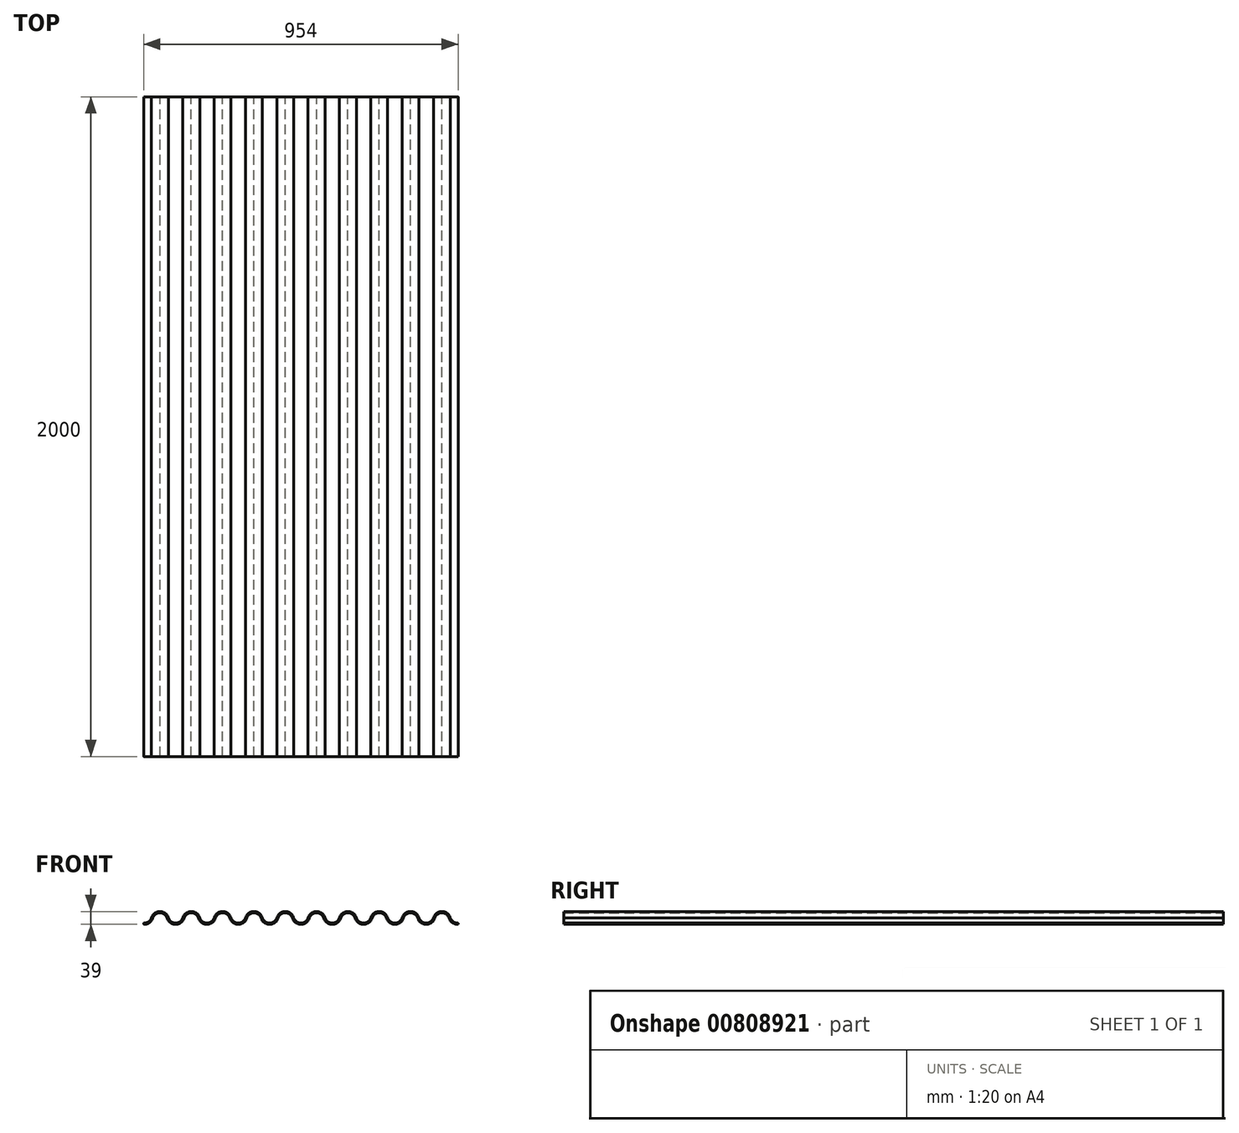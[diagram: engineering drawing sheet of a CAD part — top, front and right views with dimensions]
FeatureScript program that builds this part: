
annotation { "Feature Type Name" : "Feature", "Feature Type Description" : "" }
export const myFeature = defineFeature(function(context is Context, id is Id, definition is map)
    precondition{}
    {
        {
            var Q0;
            Q0=qCreatedBy(makeId("Front.planeOp"),FACE);
            var sketch = newSketch(context, id + "F0", { "sketchPlane" : qUnion([Q0])});
            skLineSegment(sketch, "E0.bottom", {"start": v(0, 0) * mm, "end": v(95, 0) * mm, "construction": true});
            skLineSegment(sketch, "E0.top", {"start": v(0, 35) * mm, "end": v(95, 35) * mm, "construction": true});
            skLineSegment(sketch, "E0.left", {"start": v(0, 0) * mm, "end": v(0, 35) * mm, "construction": true});
            skLineSegment(sketch, "E0.right", {"start": v(95, 0) * mm, "end": v(95, 35) * mm, "construction": true});
            skLineSegment(sketch, "E1", {"start": v(0, 17.5) * mm, "end": v(95, 17.5) * mm, "construction": true});
            skLineSegment(sketch, "E2", {"start": v(47.5, 35) * mm, "end": v(47.5, 0) * mm, "construction": true});
            skLineSegment(sketch, "E3", {"start": v(23.75, 35) * mm, "end": v(23.75, 0) * mm, "construction": true});
            skLineSegment(sketch, "E4", {"start": v(71.25, 35) * mm, "end": v(71.25, 0) * mm, "construction": true});
            skSolve(sketch);
        }
        {
            var Q0;
            Q0=qCreatedBy(makeId("Front.planeOp"),FACE);
            var sketch = newSketch(context, id + "F1", { "sketchPlane" : qUnion([Q0])});
            skArc(sketch, "E5", {"start": v(71.25, 17.2) * mm, "mid": v(62.3, 30) * mm, "end": v(47.5, 35) * mm});
            skArc(sketch, "E6", {"start": v(0, 0) * mm, "mid": v(14.66, 4.75) * mm, "end": v(23.75, 17.2) * mm});
            skArc(sketch, "E7", {"start": v(47.5, 35) * mm, "mid": v(32.7, 30) * mm, "end": v(23.75, 17.2) * mm});
            skArc(sketch, "E8", {"start": v(71.25, 17.2) * mm, "mid": v(80.34, 4.75) * mm, "end": v(95, 0) * mm});
            skArc(sketch, "E9.MirrorCS", {"start": v(0, 0) * mm, "mid": v(-14.66, 4.75) * mm, "end": v(-23.75, 17.2) * mm});
            skArc(sketch, "E10.MirrorCS", {"start": v(-71.25, 17.2) * mm, "mid": v(-80.34, 4.75) * mm, "end": v(-95, 0) * mm});
            skArc(sketch, "E11.MirrorCS", {"start": v(-47.5, 35) * mm, "mid": v(-32.7, 30) * mm, "end": v(-23.75, 17.2) * mm});
            skArc(sketch, "E12.MirrorCS", {"start": v(-71.25, 17.2) * mm, "mid": v(-62.3, 30) * mm, "end": v(-47.5, 35) * mm});
            skArc(sketch, "E13", {"start": v(261.25, 17.2) * mm, "mid": v(252.3, 30) * mm, "end": v(237.5, 35) * mm});
            skArc(sketch, "E14", {"start": v(190, 0) * mm, "mid": v(204.66, 4.75) * mm, "end": v(213.75, 17.2) * mm});
            skArc(sketch, "E15", {"start": v(237.5, 35) * mm, "mid": v(222.7, 30) * mm, "end": v(213.75, 17.2) * mm});
            skArc(sketch, "E16", {"start": v(261.25, 17.2) * mm, "mid": v(270.34, 4.75) * mm, "end": v(285, 0) * mm});
            skArc(sketch, "E17.MirrorCS", {"start": v(190, 0) * mm, "mid": v(175.34, 4.75) * mm, "end": v(166.25, 17.2) * mm});
            skArc(sketch, "E18.MirrorCS", {"start": v(118.75, 17.2) * mm, "mid": v(109.66, 4.75) * mm, "end": v(95, 0) * mm});
            skArc(sketch, "E19.MirrorCS", {"start": v(142.5, 35) * mm, "mid": v(157.3, 30) * mm, "end": v(166.25, 17.2) * mm});
            skArc(sketch, "E20.MirrorCS", {"start": v(118.75, 17.2) * mm, "mid": v(127.7, 30) * mm, "end": v(142.5, 35) * mm});
            skArc(sketch, "E21", {"start": v(451.25, 17.2) * mm, "mid": v(442.3, 30) * mm, "end": v(427.5, 35) * mm});
            skArc(sketch, "E22", {"start": v(380, 0) * mm, "mid": v(394.66, 4.75) * mm, "end": v(403.75, 17.2) * mm});
            skArc(sketch, "E23", {"start": v(427.5, 35) * mm, "mid": v(412.7, 30) * mm, "end": v(403.75, 17.2) * mm});
            skArc(sketch, "E24", {"start": v(451.25, 17.2) * mm, "mid": v(460.34, 4.75) * mm, "end": v(475, 0) * mm});
            skArc(sketch, "E25.MirrorCS", {"start": v(380, 0) * mm, "mid": v(365.34, 4.75) * mm, "end": v(356.25, 17.2) * mm});
            skArc(sketch, "E26.MirrorCS", {"start": v(308.75, 17.2) * mm, "mid": v(299.66, 4.75) * mm, "end": v(285, 0) * mm});
            skArc(sketch, "E27.MirrorCS", {"start": v(332.5, 35) * mm, "mid": v(347.3, 30) * mm, "end": v(356.25, 17.2) * mm});
            skArc(sketch, "E28.MirrorCS", {"start": v(308.75, 17.2) * mm, "mid": v(317.7, 30) * mm, "end": v(332.5, 35) * mm});
            skArc(sketch, "E29", {"start": v(641.25, 17.2) * mm, "mid": v(632.3, 30) * mm, "end": v(617.5, 35) * mm});
            skArc(sketch, "E30", {"start": v(570, 0) * mm, "mid": v(584.66, 4.75) * mm, "end": v(593.75, 17.2) * mm});
            skArc(sketch, "E31", {"start": v(617.5, 35) * mm, "mid": v(602.7, 30) * mm, "end": v(593.75, 17.2) * mm});
            skArc(sketch, "E32", {"start": v(641.25, 17.2) * mm, "mid": v(650.34, 4.75) * mm, "end": v(665, 0) * mm});
            skArc(sketch, "E33.MirrorCS", {"start": v(570, 0) * mm, "mid": v(555.34, 4.75) * mm, "end": v(546.25, 17.2) * mm});
            skArc(sketch, "E34.MirrorCS", {"start": v(498.75, 17.2) * mm, "mid": v(489.66, 4.75) * mm, "end": v(475, 0) * mm});
            skArc(sketch, "E35.MirrorCS", {"start": v(522.5, 35) * mm, "mid": v(537.3, 30) * mm, "end": v(546.25, 17.2) * mm});
            skArc(sketch, "E36.MirrorCS", {"start": v(498.75, 17.2) * mm, "mid": v(507.7, 30) * mm, "end": v(522.5, 35) * mm});
            skArc(sketch, "E37", {"start": v(831.25, 17.2) * mm, "mid": v(822.3, 30) * mm, "end": v(807.5, 35) * mm});
            skArc(sketch, "E38", {"start": v(760, 0) * mm, "mid": v(774.66, 4.75) * mm, "end": v(783.75, 17.2) * mm});
            skArc(sketch, "E39", {"start": v(807.5, 35) * mm, "mid": v(792.7, 30) * mm, "end": v(783.75, 17.2) * mm});
            skArc(sketch, "E40", {"start": v(831.25, 17.2) * mm, "mid": v(840.34, 4.75) * mm, "end": v(855, 0) * mm});
            skArc(sketch, "E41.MirrorCS", {"start": v(760, 0) * mm, "mid": v(745.34, 4.75) * mm, "end": v(736.25, 17.2) * mm});
            skArc(sketch, "E42.MirrorCS", {"start": v(688.75, 17.2) * mm, "mid": v(679.66, 4.75) * mm, "end": v(665, 0) * mm});
            skArc(sketch, "E43.MirrorCS", {"start": v(712.5, 35) * mm, "mid": v(727.3, 30) * mm, "end": v(736.25, 17.2) * mm});
            skArc(sketch, "E44.MirrorCS", {"start": v(688.75, 17.2) * mm, "mid": v(697.7, 30) * mm, "end": v(712.5, 35) * mm});
            skArc(sketch, "E45.0.startCap", {"start": v(760, 2) * mm, "mid": v(762, 0) * mm, "end": v(760, -2) * mm});
            skArc(sketch, "E45.0.endCap", {"start": v(734.35, 16.57) * mm, "mid": v(735.63, 19.1) * mm, "end": v(738.15, 17.82) * mm});
            skArc(sketch, "E45.0.left", {"start": v(760, -2) * mm, "mid": v(744.17, 3.13) * mm, "end": v(734.35, 16.57) * mm});
            skArc(sketch, "E45.0.right", {"start": v(760, 2) * mm, "mid": v(746.51, 6.37) * mm, "end": v(738.15, 17.82) * mm});
            skArc(sketch, "E45.1.startCap", {"start": v(380, 2) * mm, "mid": v(382, 0) * mm, "end": v(380, -2) * mm});
            skArc(sketch, "E45.1.endCap", {"start": v(354.35, 16.57) * mm, "mid": v(355.63, 19.1) * mm, "end": v(358.15, 17.82) * mm});
            skArc(sketch, "E45.1.left", {"start": v(380, -2) * mm, "mid": v(364.17, 3.13) * mm, "end": v(354.35, 16.57) * mm});
            skArc(sketch, "E45.1.right", {"start": v(380, 2) * mm, "mid": v(366.51, 6.37) * mm, "end": v(358.15, 17.82) * mm});
            skArc(sketch, "E45.2.startCap", {"start": v(190, 2) * mm, "mid": v(192, 0) * mm, "end": v(190, -2) * mm});
            skArc(sketch, "E45.2.endCap", {"start": v(164.35, 16.57) * mm, "mid": v(165.63, 19.1) * mm, "end": v(168.15, 17.82) * mm});
            skArc(sketch, "E45.2.left", {"start": v(190, -2) * mm, "mid": v(174.17, 3.13) * mm, "end": v(164.35, 16.57) * mm});
            skArc(sketch, "E45.2.right", {"start": v(190, 2) * mm, "mid": v(176.51, 6.37) * mm, "end": v(168.15, 17.82) * mm});
            skArc(sketch, "E45.3.startCap", {"start": v(570, 2) * mm, "mid": v(572, 0) * mm, "end": v(570, -2) * mm});
            skArc(sketch, "E45.3.endCap", {"start": v(544.35, 16.57) * mm, "mid": v(545.63, 19.1) * mm, "end": v(548.15, 17.82) * mm});
            skArc(sketch, "E45.3.left", {"start": v(570, -2) * mm, "mid": v(554.17, 3.13) * mm, "end": v(544.35, 16.57) * mm});
            skArc(sketch, "E45.3.right", {"start": v(570, 2) * mm, "mid": v(556.51, 6.37) * mm, "end": v(548.15, 17.82) * mm});
            skArc(sketch, "E45.4.startCap", {"start": v(639.35, 16.57) * mm, "mid": v(640.63, 19.1) * mm, "end": v(643.15, 17.82) * mm});
            skArc(sketch, "E45.4.endCap", {"start": v(665, 2) * mm, "mid": v(667, 0) * mm, "end": v(665, -2) * mm});
            skArc(sketch, "E45.4.left", {"start": v(643.15, 17.82) * mm, "mid": v(651.51, 6.37) * mm, "end": v(665, 2) * mm});
            skArc(sketch, "E45.4.right", {"start": v(639.35, 16.57) * mm, "mid": v(649.17, 3.13) * mm, "end": v(665, -2) * mm});
            skArc(sketch, "E45.5.startCap", {"start": v(449.35, 16.57) * mm, "mid": v(450.63, 19.1) * mm, "end": v(453.15, 17.82) * mm});
            skArc(sketch, "E45.5.endCap", {"start": v(475, 2) * mm, "mid": v(477, 0) * mm, "end": v(475, -2) * mm});
            skArc(sketch, "E45.5.left", {"start": v(453.15, 17.82) * mm, "mid": v(461.51, 6.37) * mm, "end": v(475, 2) * mm});
            skArc(sketch, "E45.5.right", {"start": v(449.35, 16.57) * mm, "mid": v(459.17, 3.13) * mm, "end": v(475, -2) * mm});
            skArc(sketch, "E45.6.startCap", {"start": v(259.35, 16.57) * mm, "mid": v(260.63, 19.1) * mm, "end": v(263.15, 17.82) * mm});
            skArc(sketch, "E45.6.endCap", {"start": v(285, 2) * mm, "mid": v(287, 0) * mm, "end": v(285, -2) * mm});
            skArc(sketch, "E45.6.left", {"start": v(263.15, 17.82) * mm, "mid": v(271.51, 6.37) * mm, "end": v(285, 2) * mm});
            skArc(sketch, "E45.6.right", {"start": v(259.35, 16.57) * mm, "mid": v(269.17, 3.13) * mm, "end": v(285, -2) * mm});
            skArc(sketch, "E45.7.startCap", {"start": v(829.35, 16.57) * mm, "mid": v(830.63, 19.1) * mm, "end": v(833.15, 17.82) * mm});
            skArc(sketch, "E45.7.endCap", {"start": v(855, 2) * mm, "mid": v(857, 0) * mm, "end": v(855, -2) * mm});
            skArc(sketch, "E45.7.left", {"start": v(833.15, 17.82) * mm, "mid": v(841.51, 6.37) * mm, "end": v(855, 2) * mm});
            skArc(sketch, "E45.7.right", {"start": v(829.35, 16.57) * mm, "mid": v(839.17, 3.13) * mm, "end": v(855, -2) * mm});
            skArc(sketch, "E45.8.startCap", {"start": v(310.67, 16.62) * mm, "mid": v(308.17, 15.28) * mm, "end": v(306.83, 17.77) * mm});
            skArc(sketch, "E45.8.endCap", {"start": v(332.48, 37) * mm, "mid": v(334.5, 35.02) * mm, "end": v(332.52, 33) * mm});
            skArc(sketch, "E45.8.left", {"start": v(306.83, 17.77) * mm, "mid": v(316.5, 31.6) * mm, "end": v(332.48, 37) * mm});
            skArc(sketch, "E45.8.right", {"start": v(310.67, 16.62) * mm, "mid": v(318.9, 28.4) * mm, "end": v(332.52, 33) * mm});
            skArc(sketch, "E45.9.startCap", {"start": v(120.67, 16.62) * mm, "mid": v(118.17, 15.28) * mm, "end": v(116.83, 17.77) * mm});
            skArc(sketch, "E45.9.endCap", {"start": v(142.48, 37) * mm, "mid": v(144.5, 35.02) * mm, "end": v(142.52, 33) * mm});
            skArc(sketch, "E45.9.left", {"start": v(116.83, 17.77) * mm, "mid": v(126.5, 31.6) * mm, "end": v(142.48, 37) * mm});
            skArc(sketch, "E45.9.right", {"start": v(120.67, 16.62) * mm, "mid": v(128.9, 28.4) * mm, "end": v(142.52, 33) * mm});
            skArc(sketch, "E45.10.startCap", {"start": v(690.67, 16.62) * mm, "mid": v(688.17, 15.28) * mm, "end": v(686.83, 17.77) * mm});
            skArc(sketch, "E45.10.endCap", {"start": v(712.48, 37) * mm, "mid": v(714.5, 35.02) * mm, "end": v(712.52, 33) * mm});
            skArc(sketch, "E45.10.left", {"start": v(686.83, 17.77) * mm, "mid": v(696.5, 31.6) * mm, "end": v(712.48, 37) * mm});
            skArc(sketch, "E45.10.right", {"start": v(690.67, 16.62) * mm, "mid": v(698.9, 28.4) * mm, "end": v(712.52, 33) * mm});
            skArc(sketch, "E45.11.startCap", {"start": v(500.67, 16.62) * mm, "mid": v(498.17, 15.28) * mm, "end": v(496.83, 17.77) * mm});
            skArc(sketch, "E45.11.endCap", {"start": v(522.48, 37) * mm, "mid": v(524.5, 35.02) * mm, "end": v(522.52, 33) * mm});
            skArc(sketch, "E45.11.left", {"start": v(496.83, 17.77) * mm, "mid": v(506.5, 31.6) * mm, "end": v(522.48, 37) * mm});
            skArc(sketch, "E45.11.right", {"start": v(500.67, 16.62) * mm, "mid": v(508.9, 28.4) * mm, "end": v(522.52, 33) * mm});
            skArc(sketch, "E45.12.startCap", {"start": v(0, 2) * mm, "mid": v(2, 0) * mm, "end": v(0, -2) * mm});
            skArc(sketch, "E45.12.endCap", {"start": v(-25.65, 16.57) * mm, "mid": v(-24.37, 19.1) * mm, "end": v(-21.85, 17.82) * mm});
            skArc(sketch, "E45.12.left", {"start": v(0, -2) * mm, "mid": v(-15.83, 3.13) * mm, "end": v(-25.65, 16.57) * mm});
            skArc(sketch, "E45.12.right", {"start": v(0, 2) * mm, "mid": v(-13.49, 6.37) * mm, "end": v(-21.85, 17.82) * mm});
            skArc(sketch, "E45.13.startCap", {"start": v(833.17, 17.77) * mm, "mid": v(831.83, 15.28) * mm, "end": v(829.33, 16.62) * mm});
            skArc(sketch, "E45.13.endCap", {"start": v(807.48, 33) * mm, "mid": v(805.5, 35.02) * mm, "end": v(807.52, 37) * mm});
            skArc(sketch, "E45.13.left", {"start": v(829.33, 16.62) * mm, "mid": v(821.1, 28.4) * mm, "end": v(807.48, 33) * mm});
            skArc(sketch, "E45.13.right", {"start": v(833.17, 17.77) * mm, "mid": v(823.5, 31.6) * mm, "end": v(807.52, 37) * mm});
            skArc(sketch, "E45.14.startCap", {"start": v(686.85, 17.82) * mm, "mid": v(689.37, 19.1) * mm, "end": v(690.65, 16.57) * mm});
            skArc(sketch, "E45.14.endCap", {"start": v(665, -2) * mm, "mid": v(663, 0) * mm, "end": v(665, 2) * mm});
            skArc(sketch, "E45.14.left", {"start": v(690.65, 16.57) * mm, "mid": v(680.83, 3.13) * mm, "end": v(665, -2) * mm});
            skArc(sketch, "E45.14.right", {"start": v(686.85, 17.82) * mm, "mid": v(678.49, 6.37) * mm, "end": v(665, 2) * mm});
            skArc(sketch, "E45.15.startCap", {"start": v(496.85, 17.82) * mm, "mid": v(499.37, 19.1) * mm, "end": v(500.65, 16.57) * mm});
            skArc(sketch, "E45.15.endCap", {"start": v(475, -2) * mm, "mid": v(473, 0) * mm, "end": v(475, 2) * mm});
            skArc(sketch, "E45.15.left", {"start": v(500.65, 16.57) * mm, "mid": v(490.83, 3.13) * mm, "end": v(475, -2) * mm});
            skArc(sketch, "E45.15.right", {"start": v(496.85, 17.82) * mm, "mid": v(488.49, 6.37) * mm, "end": v(475, 2) * mm});
            skArc(sketch, "E45.16.startCap", {"start": v(643.17, 17.77) * mm, "mid": v(641.83, 15.28) * mm, "end": v(639.33, 16.62) * mm});
            skArc(sketch, "E45.16.endCap", {"start": v(617.48, 33) * mm, "mid": v(615.5, 35.02) * mm, "end": v(617.52, 37) * mm});
            skArc(sketch, "E45.16.left", {"start": v(639.33, 16.62) * mm, "mid": v(631.1, 28.4) * mm, "end": v(617.48, 33) * mm});
            skArc(sketch, "E45.16.right", {"start": v(643.17, 17.77) * mm, "mid": v(633.5, 31.6) * mm, "end": v(617.52, 37) * mm});
            skArc(sketch, "E45.17.startCap", {"start": v(306.85, 17.82) * mm, "mid": v(309.37, 19.1) * mm, "end": v(310.65, 16.57) * mm});
            skArc(sketch, "E45.17.endCap", {"start": v(285, -2) * mm, "mid": v(283, 0) * mm, "end": v(285, 2) * mm});
            skArc(sketch, "E45.17.left", {"start": v(310.65, 16.57) * mm, "mid": v(300.83, 3.13) * mm, "end": v(285, -2) * mm});
            skArc(sketch, "E45.17.right", {"start": v(306.85, 17.82) * mm, "mid": v(298.49, 6.37) * mm, "end": v(285, 2) * mm});
            skArc(sketch, "E45.18.startCap", {"start": v(116.85, 17.82) * mm, "mid": v(119.37, 19.1) * mm, "end": v(120.65, 16.57) * mm});
            skArc(sketch, "E45.18.endCap", {"start": v(95, -2) * mm, "mid": v(93, 0) * mm, "end": v(95, 2) * mm});
            skArc(sketch, "E45.18.left", {"start": v(120.65, 16.57) * mm, "mid": v(110.83, 3.13) * mm, "end": v(95, -2) * mm});
            skArc(sketch, "E45.18.right", {"start": v(116.85, 17.82) * mm, "mid": v(108.49, 6.37) * mm, "end": v(95, 2) * mm});
            skArc(sketch, "E45.19.startCap", {"start": v(453.17, 17.77) * mm, "mid": v(451.83, 15.28) * mm, "end": v(449.33, 16.62) * mm});
            skArc(sketch, "E45.19.endCap", {"start": v(427.48, 33) * mm, "mid": v(425.5, 35.02) * mm, "end": v(427.52, 37) * mm});
            skArc(sketch, "E45.19.left", {"start": v(449.33, 16.62) * mm, "mid": v(441.1, 28.4) * mm, "end": v(427.48, 33) * mm});
            skArc(sketch, "E45.19.right", {"start": v(453.17, 17.77) * mm, "mid": v(443.5, 31.6) * mm, "end": v(427.52, 37) * mm});
            skArc(sketch, "E45.20.startCap", {"start": v(263.17, 17.77) * mm, "mid": v(261.83, 15.28) * mm, "end": v(259.33, 16.62) * mm});
            skArc(sketch, "E45.20.endCap", {"start": v(237.48, 33) * mm, "mid": v(235.5, 35.02) * mm, "end": v(237.52, 37) * mm});
            skArc(sketch, "E45.20.left", {"start": v(259.33, 16.62) * mm, "mid": v(251.1, 28.4) * mm, "end": v(237.48, 33) * mm});
            skArc(sketch, "E45.20.right", {"start": v(263.17, 17.77) * mm, "mid": v(253.5, 31.6) * mm, "end": v(237.52, 37) * mm});
            skArc(sketch, "E45.21.startCap", {"start": v(-69.33, 16.62) * mm, "mid": v(-71.83, 15.28) * mm, "end": v(-73.17, 17.77) * mm});
            skArc(sketch, "E45.21.endCap", {"start": v(-47.52, 37) * mm, "mid": v(-45.5, 35.02) * mm, "end": v(-47.48, 33) * mm});
            skArc(sketch, "E45.21.left", {"start": v(-73.17, 17.77) * mm, "mid": v(-63.5, 31.6) * mm, "end": v(-47.52, 37) * mm});
            skArc(sketch, "E45.21.right", {"start": v(-69.33, 16.62) * mm, "mid": v(-61.1, 28.4) * mm, "end": v(-47.48, 33) * mm});
            skArc(sketch, "E45.22.startCap", {"start": v(-47.52, 33) * mm, "mid": v(-49.5, 35.02) * mm, "end": v(-47.48, 37) * mm});
            skArc(sketch, "E45.22.endCap", {"start": v(-21.83, 17.77) * mm, "mid": v(-23.17, 15.28) * mm, "end": v(-25.67, 16.62) * mm});
            skArc(sketch, "E45.22.left", {"start": v(-47.48, 37) * mm, "mid": v(-31.5, 31.6) * mm, "end": v(-21.83, 17.77) * mm});
            skArc(sketch, "E45.22.right", {"start": v(-47.52, 33) * mm, "mid": v(-33.9, 28.4) * mm, "end": v(-25.67, 16.62) * mm});
            skArc(sketch, "E45.23.startCap", {"start": v(73.17, 17.77) * mm, "mid": v(71.83, 15.28) * mm, "end": v(69.33, 16.62) * mm});
            skArc(sketch, "E45.23.endCap", {"start": v(47.48, 33) * mm, "mid": v(45.5, 35.02) * mm, "end": v(47.52, 37) * mm});
            skArc(sketch, "E45.23.left", {"start": v(69.33, 16.62) * mm, "mid": v(61.1, 28.4) * mm, "end": v(47.48, 33) * mm});
            skArc(sketch, "E45.23.right", {"start": v(73.17, 17.77) * mm, "mid": v(63.5, 31.6) * mm, "end": v(47.52, 37) * mm});
            skArc(sketch, "E45.24.startCap", {"start": v(-73.15, 17.82) * mm, "mid": v(-70.63, 19.1) * mm, "end": v(-69.35, 16.57) * mm});
            skArc(sketch, "E45.24.endCap", {"start": v(-95, -2) * mm, "mid": v(-97, 0) * mm, "end": v(-95, 2) * mm});
            skArc(sketch, "E45.24.left", {"start": v(-69.35, 16.57) * mm, "mid": v(-79.17, 3.13) * mm, "end": v(-95, -2) * mm});
            skArc(sketch, "E45.24.right", {"start": v(-73.15, 17.82) * mm, "mid": v(-81.51, 6.37) * mm, "end": v(-95, 2) * mm});
            skArc(sketch, "E45.25.startCap", {"start": v(47.48, 37) * mm, "mid": v(49.5, 35.02) * mm, "end": v(47.52, 33) * mm});
            skArc(sketch, "E45.25.endCap", {"start": v(25.67, 16.62) * mm, "mid": v(23.17, 15.28) * mm, "end": v(21.83, 17.77) * mm});
            skArc(sketch, "E45.25.left", {"start": v(47.52, 33) * mm, "mid": v(33.9, 28.4) * mm, "end": v(25.67, 16.62) * mm});
            skArc(sketch, "E45.25.right", {"start": v(47.48, 37) * mm, "mid": v(31.5, 31.6) * mm, "end": v(21.83, 17.77) * mm});
            skArc(sketch, "E45.26.startCap", {"start": v(332.48, 33) * mm, "mid": v(330.5, 35.02) * mm, "end": v(332.52, 37) * mm});
            skArc(sketch, "E45.26.endCap", {"start": v(358.17, 17.77) * mm, "mid": v(356.83, 15.28) * mm, "end": v(354.33, 16.62) * mm});
            skArc(sketch, "E45.26.left", {"start": v(332.52, 37) * mm, "mid": v(348.5, 31.6) * mm, "end": v(358.17, 17.77) * mm});
            skArc(sketch, "E45.26.right", {"start": v(332.48, 33) * mm, "mid": v(346.1, 28.4) * mm, "end": v(354.33, 16.62) * mm});
            skArc(sketch, "E45.27.startCap", {"start": v(142.48, 33) * mm, "mid": v(140.5, 35.02) * mm, "end": v(142.52, 37) * mm});
            skArc(sketch, "E45.27.endCap", {"start": v(168.17, 17.77) * mm, "mid": v(166.83, 15.28) * mm, "end": v(164.33, 16.62) * mm});
            skArc(sketch, "E45.27.left", {"start": v(142.52, 37) * mm, "mid": v(158.5, 31.6) * mm, "end": v(168.17, 17.77) * mm});
            skArc(sketch, "E45.27.right", {"start": v(142.48, 33) * mm, "mid": v(156.1, 28.4) * mm, "end": v(164.33, 16.62) * mm});
            skArc(sketch, "E45.28.startCap", {"start": v(712.48, 33) * mm, "mid": v(710.5, 35.02) * mm, "end": v(712.52, 37) * mm});
            skArc(sketch, "E45.28.endCap", {"start": v(738.17, 17.77) * mm, "mid": v(736.83, 15.28) * mm, "end": v(734.33, 16.62) * mm});
            skArc(sketch, "E45.28.left", {"start": v(712.52, 37) * mm, "mid": v(728.5, 31.6) * mm, "end": v(738.17, 17.77) * mm});
            skArc(sketch, "E45.28.right", {"start": v(712.48, 33) * mm, "mid": v(726.1, 28.4) * mm, "end": v(734.33, 16.62) * mm});
            skArc(sketch, "E45.29.startCap", {"start": v(522.48, 33) * mm, "mid": v(520.5, 35.02) * mm, "end": v(522.52, 37) * mm});
            skArc(sketch, "E45.29.endCap", {"start": v(548.17, 17.77) * mm, "mid": v(546.83, 15.28) * mm, "end": v(544.33, 16.62) * mm});
            skArc(sketch, "E45.29.left", {"start": v(522.52, 37) * mm, "mid": v(538.5, 31.6) * mm, "end": v(548.17, 17.77) * mm});
            skArc(sketch, "E45.29.right", {"start": v(522.48, 33) * mm, "mid": v(536.1, 28.4) * mm, "end": v(544.33, 16.62) * mm});
            skArc(sketch, "E45.30.startCap", {"start": v(380, -2) * mm, "mid": v(378, 0) * mm, "end": v(380, 2) * mm});
            skArc(sketch, "E45.30.endCap", {"start": v(401.85, 17.82) * mm, "mid": v(404.37, 19.1) * mm, "end": v(405.65, 16.57) * mm});
            skArc(sketch, "E45.30.left", {"start": v(380, 2) * mm, "mid": v(393.49, 6.37) * mm, "end": v(401.85, 17.82) * mm});
            skArc(sketch, "E45.30.right", {"start": v(380, -2) * mm, "mid": v(395.83, 3.13) * mm, "end": v(405.65, 16.57) * mm});
            skArc(sketch, "E45.31.startCap", {"start": v(190, -2) * mm, "mid": v(188, 0) * mm, "end": v(190, 2) * mm});
            skArc(sketch, "E45.31.endCap", {"start": v(211.85, 17.82) * mm, "mid": v(214.37, 19.1) * mm, "end": v(215.65, 16.57) * mm});
            skArc(sketch, "E45.31.left", {"start": v(190, 2) * mm, "mid": v(203.49, 6.37) * mm, "end": v(211.85, 17.82) * mm});
            skArc(sketch, "E45.31.right", {"start": v(190, -2) * mm, "mid": v(205.83, 3.13) * mm, "end": v(215.65, 16.57) * mm});
            skArc(sketch, "E45.32.startCap", {"start": v(760, -2) * mm, "mid": v(758, 0) * mm, "end": v(760, 2) * mm});
            skArc(sketch, "E45.32.endCap", {"start": v(781.85, 17.82) * mm, "mid": v(784.37, 19.1) * mm, "end": v(785.65, 16.57) * mm});
            skArc(sketch, "E45.32.left", {"start": v(760, 2) * mm, "mid": v(773.49, 6.37) * mm, "end": v(781.85, 17.82) * mm});
            skArc(sketch, "E45.32.right", {"start": v(760, -2) * mm, "mid": v(775.83, 3.13) * mm, "end": v(785.65, 16.57) * mm});
            skArc(sketch, "E45.33.startCap", {"start": v(570, -2) * mm, "mid": v(568, 0) * mm, "end": v(570, 2) * mm});
            skArc(sketch, "E45.33.endCap", {"start": v(591.85, 17.82) * mm, "mid": v(594.37, 19.1) * mm, "end": v(595.65, 16.57) * mm});
            skArc(sketch, "E45.33.left", {"start": v(570, 2) * mm, "mid": v(583.49, 6.37) * mm, "end": v(591.85, 17.82) * mm});
            skArc(sketch, "E45.33.right", {"start": v(570, -2) * mm, "mid": v(585.83, 3.13) * mm, "end": v(595.65, 16.57) * mm});
            skArc(sketch, "E45.34.startCap", {"start": v(807.48, 37) * mm, "mid": v(809.5, 35.02) * mm, "end": v(807.52, 33) * mm});
            skArc(sketch, "E45.34.endCap", {"start": v(785.67, 16.62) * mm, "mid": v(783.17, 15.28) * mm, "end": v(781.83, 17.77) * mm});
            skArc(sketch, "E45.34.left", {"start": v(807.52, 33) * mm, "mid": v(793.9, 28.4) * mm, "end": v(785.67, 16.62) * mm});
            skArc(sketch, "E45.34.right", {"start": v(807.48, 37) * mm, "mid": v(791.5, 31.6) * mm, "end": v(781.83, 17.77) * mm});
            skArc(sketch, "E45.35.startCap", {"start": v(617.48, 37) * mm, "mid": v(619.5, 35.02) * mm, "end": v(617.52, 33) * mm});
            skArc(sketch, "E45.35.endCap", {"start": v(595.67, 16.62) * mm, "mid": v(593.17, 15.28) * mm, "end": v(591.83, 17.77) * mm});
            skArc(sketch, "E45.35.left", {"start": v(617.52, 33) * mm, "mid": v(603.9, 28.4) * mm, "end": v(595.67, 16.62) * mm});
            skArc(sketch, "E45.35.right", {"start": v(617.48, 37) * mm, "mid": v(601.5, 31.6) * mm, "end": v(591.83, 17.77) * mm});
            skArc(sketch, "E45.36.startCap", {"start": v(427.48, 37) * mm, "mid": v(429.5, 35.02) * mm, "end": v(427.52, 33) * mm});
            skArc(sketch, "E45.36.endCap", {"start": v(405.67, 16.62) * mm, "mid": v(403.17, 15.28) * mm, "end": v(401.83, 17.77) * mm});
            skArc(sketch, "E45.36.left", {"start": v(427.52, 33) * mm, "mid": v(413.9, 28.4) * mm, "end": v(405.67, 16.62) * mm});
            skArc(sketch, "E45.36.right", {"start": v(427.48, 37) * mm, "mid": v(411.5, 31.6) * mm, "end": v(401.83, 17.77) * mm});
            skArc(sketch, "E45.37.startCap", {"start": v(237.48, 37) * mm, "mid": v(239.5, 35.02) * mm, "end": v(237.52, 33) * mm});
            skArc(sketch, "E45.37.endCap", {"start": v(215.67, 16.62) * mm, "mid": v(213.17, 15.28) * mm, "end": v(211.83, 17.77) * mm});
            skArc(sketch, "E45.37.left", {"start": v(237.52, 33) * mm, "mid": v(223.9, 28.4) * mm, "end": v(215.67, 16.62) * mm});
            skArc(sketch, "E45.37.right", {"start": v(237.48, 37) * mm, "mid": v(221.5, 31.6) * mm, "end": v(211.83, 17.77) * mm});
            skArc(sketch, "E45.38.startCap", {"start": v(116.85, 17.82) * mm, "mid": v(119.37, 19.1) * mm, "end": v(120.65, 16.57) * mm});
            skArc(sketch, "E45.38.endCap", {"start": v(95, -2) * mm, "mid": v(93, 0) * mm, "end": v(95, 2) * mm});
            skArc(sketch, "E45.38.left", {"start": v(120.65, 16.57) * mm, "mid": v(110.83, 3.13) * mm, "end": v(95, -2) * mm});
            skArc(sketch, "E45.38.right", {"start": v(116.85, 17.82) * mm, "mid": v(108.49, 6.37) * mm, "end": v(95, 2) * mm});
            skArc(sketch, "E45.39.startCap", {"start": v(142.48, 33) * mm, "mid": v(140.5, 35.02) * mm, "end": v(142.52, 37) * mm});
            skArc(sketch, "E45.39.endCap", {"start": v(168.17, 17.77) * mm, "mid": v(166.83, 15.28) * mm, "end": v(164.33, 16.62) * mm});
            skArc(sketch, "E45.39.left", {"start": v(142.52, 37) * mm, "mid": v(158.5, 31.6) * mm, "end": v(168.17, 17.77) * mm});
            skArc(sketch, "E45.39.right", {"start": v(142.48, 33) * mm, "mid": v(156.1, 28.4) * mm, "end": v(164.33, 16.62) * mm});
            skArc(sketch, "E45.40.startCap", {"start": v(332.48, 33) * mm, "mid": v(330.5, 35.02) * mm, "end": v(332.52, 37) * mm});
            skArc(sketch, "E45.40.endCap", {"start": v(358.17, 17.77) * mm, "mid": v(356.83, 15.28) * mm, "end": v(354.33, 16.62) * mm});
            skArc(sketch, "E45.40.left", {"start": v(332.52, 37) * mm, "mid": v(348.5, 31.6) * mm, "end": v(358.17, 17.77) * mm});
            skArc(sketch, "E45.40.right", {"start": v(332.48, 33) * mm, "mid": v(346.1, 28.4) * mm, "end": v(354.33, 16.62) * mm});
            skArc(sketch, "E45.41.startCap", {"start": v(712.48, 33) * mm, "mid": v(710.5, 35.02) * mm, "end": v(712.52, 37) * mm});
            skArc(sketch, "E45.41.endCap", {"start": v(738.17, 17.77) * mm, "mid": v(736.83, 15.28) * mm, "end": v(734.33, 16.62) * mm});
            skArc(sketch, "E45.41.left", {"start": v(712.52, 37) * mm, "mid": v(728.5, 31.6) * mm, "end": v(738.17, 17.77) * mm});
            skArc(sketch, "E45.41.right", {"start": v(712.48, 33) * mm, "mid": v(726.1, 28.4) * mm, "end": v(734.33, 16.62) * mm});
            skArc(sketch, "E45.42.startCap", {"start": v(449.35, 16.57) * mm, "mid": v(450.63, 19.1) * mm, "end": v(453.15, 17.82) * mm});
            skArc(sketch, "E45.42.endCap", {"start": v(475, 2) * mm, "mid": v(477, 0) * mm, "end": v(475, -2) * mm});
            skArc(sketch, "E45.42.left", {"start": v(453.15, 17.82) * mm, "mid": v(461.51, 6.37) * mm, "end": v(475, 2) * mm});
            skArc(sketch, "E45.42.right", {"start": v(449.35, 16.57) * mm, "mid": v(459.17, 3.13) * mm, "end": v(475, -2) * mm});
            skArc(sketch, "E45.43.startCap", {"start": v(522.48, 33) * mm, "mid": v(520.5, 35.02) * mm, "end": v(522.52, 37) * mm});
            skArc(sketch, "E45.43.endCap", {"start": v(548.17, 17.77) * mm, "mid": v(546.83, 15.28) * mm, "end": v(544.33, 16.62) * mm});
            skArc(sketch, "E45.43.left", {"start": v(522.52, 37) * mm, "mid": v(538.5, 31.6) * mm, "end": v(548.17, 17.77) * mm});
            skArc(sketch, "E45.43.right", {"start": v(522.48, 33) * mm, "mid": v(536.1, 28.4) * mm, "end": v(544.33, 16.62) * mm});
            skArc(sketch, "E45.44.startCap", {"start": v(639.35, 16.57) * mm, "mid": v(640.63, 19.1) * mm, "end": v(643.15, 17.82) * mm});
            skArc(sketch, "E45.44.endCap", {"start": v(665, 2) * mm, "mid": v(667, 0) * mm, "end": v(665, -2) * mm});
            skArc(sketch, "E45.44.left", {"start": v(643.15, 17.82) * mm, "mid": v(651.51, 6.37) * mm, "end": v(665, 2) * mm});
            skArc(sketch, "E45.44.right", {"start": v(639.35, 16.57) * mm, "mid": v(649.17, 3.13) * mm, "end": v(665, -2) * mm});
            skArc(sketch, "E45.45.startCap", {"start": v(829.35, 16.57) * mm, "mid": v(830.63, 19.1) * mm, "end": v(833.15, 17.82) * mm});
            skArc(sketch, "E45.45.endCap", {"start": v(855, 2) * mm, "mid": v(857, 0) * mm, "end": v(855, -2) * mm});
            skArc(sketch, "E45.45.left", {"start": v(833.15, 17.82) * mm, "mid": v(841.51, 6.37) * mm, "end": v(855, 2) * mm});
            skArc(sketch, "E45.45.right", {"start": v(829.35, 16.57) * mm, "mid": v(839.17, 3.13) * mm, "end": v(855, -2) * mm});
            skArc(sketch, "E45.46.startCap", {"start": v(306.85, 17.82) * mm, "mid": v(309.37, 19.1) * mm, "end": v(310.65, 16.57) * mm});
            skArc(sketch, "E45.46.endCap", {"start": v(285, -2) * mm, "mid": v(283, 0) * mm, "end": v(285, 2) * mm});
            skArc(sketch, "E45.46.left", {"start": v(310.65, 16.57) * mm, "mid": v(300.83, 3.13) * mm, "end": v(285, -2) * mm});
            skArc(sketch, "E45.46.right", {"start": v(306.85, 17.82) * mm, "mid": v(298.49, 6.37) * mm, "end": v(285, 2) * mm});
            skArc(sketch, "E45.47.startCap", {"start": v(833.17, 17.77) * mm, "mid": v(831.83, 15.28) * mm, "end": v(829.33, 16.62) * mm});
            skArc(sketch, "E45.47.endCap", {"start": v(807.48, 33) * mm, "mid": v(805.5, 35.02) * mm, "end": v(807.52, 37) * mm});
            skArc(sketch, "E45.47.left", {"start": v(829.33, 16.62) * mm, "mid": v(821.1, 28.4) * mm, "end": v(807.48, 33) * mm});
            skArc(sketch, "E45.47.right", {"start": v(833.17, 17.77) * mm, "mid": v(823.5, 31.6) * mm, "end": v(807.52, 37) * mm});
            skArc(sketch, "E45.48.startCap", {"start": v(643.17, 17.77) * mm, "mid": v(641.83, 15.28) * mm, "end": v(639.33, 16.62) * mm});
            skArc(sketch, "E45.48.endCap", {"start": v(617.48, 33) * mm, "mid": v(615.5, 35.02) * mm, "end": v(617.52, 37) * mm});
            skArc(sketch, "E45.48.left", {"start": v(639.33, 16.62) * mm, "mid": v(631.1, 28.4) * mm, "end": v(617.48, 33) * mm});
            skArc(sketch, "E45.48.right", {"start": v(643.17, 17.77) * mm, "mid": v(633.5, 31.6) * mm, "end": v(617.52, 37) * mm});
            skArc(sketch, "E45.49.startCap", {"start": v(263.17, 17.77) * mm, "mid": v(261.83, 15.28) * mm, "end": v(259.33, 16.62) * mm});
            skArc(sketch, "E45.49.endCap", {"start": v(237.48, 33) * mm, "mid": v(235.5, 35.02) * mm, "end": v(237.52, 37) * mm});
            skArc(sketch, "E45.49.left", {"start": v(259.33, 16.62) * mm, "mid": v(251.1, 28.4) * mm, "end": v(237.48, 33) * mm});
            skArc(sketch, "E45.49.right", {"start": v(263.17, 17.77) * mm, "mid": v(253.5, 31.6) * mm, "end": v(237.52, 37) * mm});
            skArc(sketch, "E45.50.startCap", {"start": v(453.17, 17.77) * mm, "mid": v(451.83, 15.28) * mm, "end": v(449.33, 16.62) * mm});
            skArc(sketch, "E45.50.endCap", {"start": v(427.48, 33) * mm, "mid": v(425.5, 35.02) * mm, "end": v(427.52, 37) * mm});
            skArc(sketch, "E45.50.left", {"start": v(449.33, 16.62) * mm, "mid": v(441.1, 28.4) * mm, "end": v(427.48, 33) * mm});
            skArc(sketch, "E45.50.right", {"start": v(453.17, 17.77) * mm, "mid": v(443.5, 31.6) * mm, "end": v(427.52, 37) * mm});
            skArc(sketch, "E45.51.startCap", {"start": v(259.35, 16.57) * mm, "mid": v(260.63, 19.1) * mm, "end": v(263.15, 17.82) * mm});
            skArc(sketch, "E45.51.endCap", {"start": v(285, 2) * mm, "mid": v(287, 0) * mm, "end": v(285, -2) * mm});
            skArc(sketch, "E45.51.left", {"start": v(263.15, 17.82) * mm, "mid": v(271.51, 6.37) * mm, "end": v(285, 2) * mm});
            skArc(sketch, "E45.51.right", {"start": v(259.35, 16.57) * mm, "mid": v(269.17, 3.13) * mm, "end": v(285, -2) * mm});
            skArc(sketch, "E45.52.startCap", {"start": v(686.85, 17.82) * mm, "mid": v(689.37, 19.1) * mm, "end": v(690.65, 16.57) * mm});
            skArc(sketch, "E45.52.endCap", {"start": v(665, -2) * mm, "mid": v(663, 0) * mm, "end": v(665, 2) * mm});
            skArc(sketch, "E45.52.left", {"start": v(690.65, 16.57) * mm, "mid": v(680.83, 3.13) * mm, "end": v(665, -2) * mm});
            skArc(sketch, "E45.52.right", {"start": v(686.85, 17.82) * mm, "mid": v(678.49, 6.37) * mm, "end": v(665, 2) * mm});
            skArc(sketch, "E45.53.startCap", {"start": v(496.85, 17.82) * mm, "mid": v(499.37, 19.1) * mm, "end": v(500.65, 16.57) * mm});
            skArc(sketch, "E45.53.endCap", {"start": v(475, -2) * mm, "mid": v(473, 0) * mm, "end": v(475, 2) * mm});
            skArc(sketch, "E45.53.left", {"start": v(500.65, 16.57) * mm, "mid": v(490.83, 3.13) * mm, "end": v(475, -2) * mm});
            skArc(sketch, "E45.53.right", {"start": v(496.85, 17.82) * mm, "mid": v(488.49, 6.37) * mm, "end": v(475, 2) * mm});
            skArc(sketch, "E45.54.startCap", {"start": v(760, 2) * mm, "mid": v(762, 0) * mm, "end": v(760, -2) * mm});
            skArc(sketch, "E45.54.endCap", {"start": v(734.35, 16.57) * mm, "mid": v(735.63, 19.1) * mm, "end": v(738.15, 17.82) * mm});
            skArc(sketch, "E45.54.left", {"start": v(760, -2) * mm, "mid": v(744.17, 3.13) * mm, "end": v(734.35, 16.57) * mm});
            skArc(sketch, "E45.54.right", {"start": v(760, 2) * mm, "mid": v(746.51, 6.37) * mm, "end": v(738.15, 17.82) * mm});
            skArc(sketch, "E45.55.startCap", {"start": v(570, 2) * mm, "mid": v(572, 0) * mm, "end": v(570, -2) * mm});
            skArc(sketch, "E45.55.endCap", {"start": v(544.35, 16.57) * mm, "mid": v(545.63, 19.1) * mm, "end": v(548.15, 17.82) * mm});
            skArc(sketch, "E45.55.left", {"start": v(570, -2) * mm, "mid": v(554.17, 3.13) * mm, "end": v(544.35, 16.57) * mm});
            skArc(sketch, "E45.55.right", {"start": v(570, 2) * mm, "mid": v(556.51, 6.37) * mm, "end": v(548.15, 17.82) * mm});
            skArc(sketch, "E45.56.startCap", {"start": v(380, 2) * mm, "mid": v(382, 0) * mm, "end": v(380, -2) * mm});
            skArc(sketch, "E45.56.endCap", {"start": v(354.35, 16.57) * mm, "mid": v(355.63, 19.1) * mm, "end": v(358.15, 17.82) * mm});
            skArc(sketch, "E45.56.left", {"start": v(380, -2) * mm, "mid": v(364.17, 3.13) * mm, "end": v(354.35, 16.57) * mm});
            skArc(sketch, "E45.56.right", {"start": v(380, 2) * mm, "mid": v(366.51, 6.37) * mm, "end": v(358.15, 17.82) * mm});
            skArc(sketch, "E45.57.startCap", {"start": v(190, 2) * mm, "mid": v(192, 0) * mm, "end": v(190, -2) * mm});
            skArc(sketch, "E45.57.endCap", {"start": v(164.35, 16.57) * mm, "mid": v(165.63, 19.1) * mm, "end": v(168.15, 17.82) * mm});
            skArc(sketch, "E45.57.left", {"start": v(190, -2) * mm, "mid": v(174.17, 3.13) * mm, "end": v(164.35, 16.57) * mm});
            skArc(sketch, "E45.57.right", {"start": v(190, 2) * mm, "mid": v(176.51, 6.37) * mm, "end": v(168.15, 17.82) * mm});
            skArc(sketch, "E45.58.startCap", {"start": v(-69.33, 16.62) * mm, "mid": v(-71.83, 15.28) * mm, "end": v(-73.17, 17.77) * mm});
            skArc(sketch, "E45.58.endCap", {"start": v(-47.52, 37) * mm, "mid": v(-45.5, 35.02) * mm, "end": v(-47.48, 33) * mm});
            skArc(sketch, "E45.58.left", {"start": v(-73.17, 17.77) * mm, "mid": v(-63.5, 31.6) * mm, "end": v(-47.52, 37) * mm});
            skArc(sketch, "E45.58.right", {"start": v(-69.33, 16.62) * mm, "mid": v(-61.1, 28.4) * mm, "end": v(-47.48, 33) * mm});
            skArc(sketch, "E45.59.startCap", {"start": v(0, 2) * mm, "mid": v(2, 0) * mm, "end": v(0, -2) * mm});
            skArc(sketch, "E45.59.endCap", {"start": v(-25.65, 16.57) * mm, "mid": v(-24.37, 19.1) * mm, "end": v(-21.85, 17.82) * mm});
            skArc(sketch, "E45.59.left", {"start": v(0, -2) * mm, "mid": v(-15.83, 3.13) * mm, "end": v(-25.65, 16.57) * mm});
            skArc(sketch, "E45.59.right", {"start": v(0, 2) * mm, "mid": v(-13.49, 6.37) * mm, "end": v(-21.85, 17.82) * mm});
            skArc(sketch, "E45.60.startCap", {"start": v(73.17, 17.77) * mm, "mid": v(71.83, 15.28) * mm, "end": v(69.33, 16.62) * mm});
            skArc(sketch, "E45.60.endCap", {"start": v(47.48, 33) * mm, "mid": v(45.5, 35.02) * mm, "end": v(47.52, 37) * mm});
            skArc(sketch, "E45.60.left", {"start": v(69.33, 16.62) * mm, "mid": v(61.1, 28.4) * mm, "end": v(47.48, 33) * mm});
            skArc(sketch, "E45.60.right", {"start": v(73.17, 17.77) * mm, "mid": v(63.5, 31.6) * mm, "end": v(47.52, 37) * mm});
            skArc(sketch, "E45.61.startCap", {"start": v(47.48, 37) * mm, "mid": v(49.5, 35.02) * mm, "end": v(47.52, 33) * mm});
            skArc(sketch, "E45.61.endCap", {"start": v(25.67, 16.62) * mm, "mid": v(23.17, 15.28) * mm, "end": v(21.83, 17.77) * mm});
            skArc(sketch, "E45.61.left", {"start": v(47.52, 33) * mm, "mid": v(33.9, 28.4) * mm, "end": v(25.67, 16.62) * mm});
            skArc(sketch, "E45.61.right", {"start": v(47.48, 37) * mm, "mid": v(31.5, 31.6) * mm, "end": v(21.83, 17.77) * mm});
            skArc(sketch, "E45.62.startCap", {"start": v(69.35, 16.57) * mm, "mid": v(70.63, 19.1) * mm, "end": v(73.15, 17.82) * mm});
            skArc(sketch, "E45.62.endCap", {"start": v(95, 2) * mm, "mid": v(97, 0) * mm, "end": v(95, -2) * mm});
            skArc(sketch, "E45.62.left", {"start": v(73.15, 17.82) * mm, "mid": v(81.51, 6.37) * mm, "end": v(95, 2) * mm});
            skArc(sketch, "E45.62.right", {"start": v(69.35, 16.57) * mm, "mid": v(79.17, 3.13) * mm, "end": v(95, -2) * mm});
            skArc(sketch, "E45.63.startCap", {"start": v(-73.15, 17.82) * mm, "mid": v(-70.63, 19.1) * mm, "end": v(-69.35, 16.57) * mm});
            skArc(sketch, "E45.63.endCap", {"start": v(-95, -2) * mm, "mid": v(-97, 0) * mm, "end": v(-95, 2) * mm});
            skArc(sketch, "E45.63.left", {"start": v(-69.35, 16.57) * mm, "mid": v(-79.17, 3.13) * mm, "end": v(-95, -2) * mm});
            skArc(sketch, "E45.63.right", {"start": v(-73.15, 17.82) * mm, "mid": v(-81.51, 6.37) * mm, "end": v(-95, 2) * mm});
            skArc(sketch, "E45.64.startCap", {"start": v(427.48, 37) * mm, "mid": v(429.5, 35.02) * mm, "end": v(427.52, 33) * mm});
            skArc(sketch, "E45.64.endCap", {"start": v(405.67, 16.62) * mm, "mid": v(403.17, 15.28) * mm, "end": v(401.83, 17.77) * mm});
            skArc(sketch, "E45.64.left", {"start": v(427.52, 33) * mm, "mid": v(413.9, 28.4) * mm, "end": v(405.67, 16.62) * mm});
            skArc(sketch, "E45.64.right", {"start": v(427.48, 37) * mm, "mid": v(411.5, 31.6) * mm, "end": v(401.83, 17.77) * mm});
            skArc(sketch, "E45.65.startCap", {"start": v(237.48, 37) * mm, "mid": v(239.5, 35.02) * mm, "end": v(237.52, 33) * mm});
            skArc(sketch, "E45.65.endCap", {"start": v(215.67, 16.62) * mm, "mid": v(213.17, 15.28) * mm, "end": v(211.83, 17.77) * mm});
            skArc(sketch, "E45.65.left", {"start": v(237.52, 33) * mm, "mid": v(223.9, 28.4) * mm, "end": v(215.67, 16.62) * mm});
            skArc(sketch, "E45.65.right", {"start": v(237.48, 37) * mm, "mid": v(221.5, 31.6) * mm, "end": v(211.83, 17.77) * mm});
            skArc(sketch, "E45.66.startCap", {"start": v(807.48, 37) * mm, "mid": v(809.5, 35.02) * mm, "end": v(807.52, 33) * mm});
            skArc(sketch, "E45.66.endCap", {"start": v(785.67, 16.62) * mm, "mid": v(783.17, 15.28) * mm, "end": v(781.83, 17.77) * mm});
            skArc(sketch, "E45.66.left", {"start": v(807.52, 33) * mm, "mid": v(793.9, 28.4) * mm, "end": v(785.67, 16.62) * mm});
            skArc(sketch, "E45.66.right", {"start": v(807.48, 37) * mm, "mid": v(791.5, 31.6) * mm, "end": v(781.83, 17.77) * mm});
            skArc(sketch, "E45.67.startCap", {"start": v(617.48, 37) * mm, "mid": v(619.5, 35.02) * mm, "end": v(617.52, 33) * mm});
            skArc(sketch, "E45.67.endCap", {"start": v(595.67, 16.62) * mm, "mid": v(593.17, 15.28) * mm, "end": v(591.83, 17.77) * mm});
            skArc(sketch, "E45.67.left", {"start": v(617.52, 33) * mm, "mid": v(603.9, 28.4) * mm, "end": v(595.67, 16.62) * mm});
            skArc(sketch, "E45.67.right", {"start": v(617.48, 37) * mm, "mid": v(601.5, 31.6) * mm, "end": v(591.83, 17.77) * mm});
            skArc(sketch, "E45.68.startCap", {"start": v(500.67, 16.62) * mm, "mid": v(498.17, 15.28) * mm, "end": v(496.83, 17.77) * mm});
            skArc(sketch, "E45.68.endCap", {"start": v(522.48, 37) * mm, "mid": v(524.5, 35.02) * mm, "end": v(522.52, 33) * mm});
            skArc(sketch, "E45.68.left", {"start": v(496.83, 17.77) * mm, "mid": v(506.5, 31.6) * mm, "end": v(522.48, 37) * mm});
            skArc(sketch, "E45.68.right", {"start": v(500.67, 16.62) * mm, "mid": v(508.9, 28.4) * mm, "end": v(522.52, 33) * mm});
            skArc(sketch, "E45.69.startCap", {"start": v(310.67, 16.62) * mm, "mid": v(308.17, 15.28) * mm, "end": v(306.83, 17.77) * mm});
            skArc(sketch, "E45.69.endCap", {"start": v(332.48, 37) * mm, "mid": v(334.5, 35.02) * mm, "end": v(332.52, 33) * mm});
            skArc(sketch, "E45.69.left", {"start": v(306.83, 17.77) * mm, "mid": v(316.5, 31.6) * mm, "end": v(332.48, 37) * mm});
            skArc(sketch, "E45.69.right", {"start": v(310.67, 16.62) * mm, "mid": v(318.9, 28.4) * mm, "end": v(332.52, 33) * mm});
            skArc(sketch, "E45.70.startCap", {"start": v(-47.52, 33) * mm, "mid": v(-49.5, 35.02) * mm, "end": v(-47.48, 37) * mm});
            skArc(sketch, "E45.70.endCap", {"start": v(-21.83, 17.77) * mm, "mid": v(-23.17, 15.28) * mm, "end": v(-25.67, 16.62) * mm});
            skArc(sketch, "E45.70.left", {"start": v(-47.48, 37) * mm, "mid": v(-31.5, 31.6) * mm, "end": v(-21.83, 17.77) * mm});
            skArc(sketch, "E45.70.right", {"start": v(-47.52, 33) * mm, "mid": v(-33.9, 28.4) * mm, "end": v(-25.67, 16.62) * mm});
            skArc(sketch, "E45.71.startCap", {"start": v(120.67, 16.62) * mm, "mid": v(118.17, 15.28) * mm, "end": v(116.83, 17.77) * mm});
            skArc(sketch, "E45.71.endCap", {"start": v(142.48, 37) * mm, "mid": v(144.5, 35.02) * mm, "end": v(142.52, 33) * mm});
            skArc(sketch, "E45.71.left", {"start": v(116.83, 17.77) * mm, "mid": v(126.5, 31.6) * mm, "end": v(142.48, 37) * mm});
            skArc(sketch, "E45.71.right", {"start": v(120.67, 16.62) * mm, "mid": v(128.9, 28.4) * mm, "end": v(142.52, 33) * mm});
            skArc(sketch, "E45.72.startCap", {"start": v(690.67, 16.62) * mm, "mid": v(688.17, 15.28) * mm, "end": v(686.83, 17.77) * mm});
            skArc(sketch, "E45.72.endCap", {"start": v(712.48, 37) * mm, "mid": v(714.5, 35.02) * mm, "end": v(712.52, 33) * mm});
            skArc(sketch, "E45.72.left", {"start": v(686.83, 17.77) * mm, "mid": v(696.5, 31.6) * mm, "end": v(712.48, 37) * mm});
            skArc(sketch, "E45.72.right", {"start": v(690.67, 16.62) * mm, "mid": v(698.9, 28.4) * mm, "end": v(712.52, 33) * mm});
            skArc(sketch, "E45.73.startCap", {"start": v(0, -2) * mm, "mid": v(-2, 0) * mm, "end": v(0, 2) * mm});
            skArc(sketch, "E45.73.endCap", {"start": v(21.85, 17.82) * mm, "mid": v(24.37, 19.1) * mm, "end": v(25.65, 16.57) * mm});
            skArc(sketch, "E45.73.left", {"start": v(0, 2) * mm, "mid": v(13.49, 6.37) * mm, "end": v(21.85, 17.82) * mm});
            skArc(sketch, "E45.73.right", {"start": v(0, -2) * mm, "mid": v(15.83, 3.13) * mm, "end": v(25.65, 16.57) * mm});
            skArc(sketch, "E45.74.startCap", {"start": v(760, -2) * mm, "mid": v(758, 0) * mm, "end": v(760, 2) * mm});
            skArc(sketch, "E45.74.endCap", {"start": v(781.85, 17.82) * mm, "mid": v(784.37, 19.1) * mm, "end": v(785.65, 16.57) * mm});
            skArc(sketch, "E45.74.left", {"start": v(760, 2) * mm, "mid": v(773.49, 6.37) * mm, "end": v(781.85, 17.82) * mm});
            skArc(sketch, "E45.74.right", {"start": v(760, -2) * mm, "mid": v(775.83, 3.13) * mm, "end": v(785.65, 16.57) * mm});
            skArc(sketch, "E45.75.startCap", {"start": v(570, -2) * mm, "mid": v(568, 0) * mm, "end": v(570, 2) * mm});
            skArc(sketch, "E45.75.endCap", {"start": v(591.85, 17.82) * mm, "mid": v(594.37, 19.1) * mm, "end": v(595.65, 16.57) * mm});
            skArc(sketch, "E45.75.left", {"start": v(570, 2) * mm, "mid": v(583.49, 6.37) * mm, "end": v(591.85, 17.82) * mm});
            skArc(sketch, "E45.75.right", {"start": v(570, -2) * mm, "mid": v(585.83, 3.13) * mm, "end": v(595.65, 16.57) * mm});
            skArc(sketch, "E45.76.startCap", {"start": v(380, -2) * mm, "mid": v(378, 0) * mm, "end": v(380, 2) * mm});
            skArc(sketch, "E45.76.endCap", {"start": v(401.85, 17.82) * mm, "mid": v(404.37, 19.1) * mm, "end": v(405.65, 16.57) * mm});
            skArc(sketch, "E45.76.left", {"start": v(380, 2) * mm, "mid": v(393.49, 6.37) * mm, "end": v(401.85, 17.82) * mm});
            skArc(sketch, "E45.76.right", {"start": v(380, -2) * mm, "mid": v(395.83, 3.13) * mm, "end": v(405.65, 16.57) * mm});
            skArc(sketch, "E45.77.startCap", {"start": v(190, -2) * mm, "mid": v(188, 0) * mm, "end": v(190, 2) * mm});
            skArc(sketch, "E45.77.endCap", {"start": v(211.85, 17.82) * mm, "mid": v(214.37, 19.1) * mm, "end": v(215.65, 16.57) * mm});
            skArc(sketch, "E45.77.left", {"start": v(190, 2) * mm, "mid": v(203.49, 6.37) * mm, "end": v(211.85, 17.82) * mm});
            skArc(sketch, "E45.77.right", {"start": v(190, -2) * mm, "mid": v(205.83, 3.13) * mm, "end": v(215.65, 16.57) * mm});
            skArc(sketch, "E45.78.startCap", {"start": v(69.35, 16.57) * mm, "mid": v(70.63, 19.1) * mm, "end": v(73.15, 17.82) * mm});
            skArc(sketch, "E45.78.endCap", {"start": v(95, 2) * mm, "mid": v(97, 0) * mm, "end": v(95, -2) * mm});
            skArc(sketch, "E45.78.left", {"start": v(73.15, 17.82) * mm, "mid": v(81.51, 6.37) * mm, "end": v(95, 2) * mm});
            skArc(sketch, "E45.78.right", {"start": v(69.35, 16.57) * mm, "mid": v(79.17, 3.13) * mm, "end": v(95, -2) * mm});
            skArc(sketch, "E45.79.startCap", {"start": v(0, -2) * mm, "mid": v(-2, 0) * mm, "end": v(0, 2) * mm});
            skArc(sketch, "E45.79.endCap", {"start": v(21.85, 17.82) * mm, "mid": v(24.37, 19.1) * mm, "end": v(25.65, 16.57) * mm});
            skArc(sketch, "E45.79.left", {"start": v(0, 2) * mm, "mid": v(13.49, 6.37) * mm, "end": v(21.85, 17.82) * mm});
            skArc(sketch, "E45.79.right", {"start": v(0, -2) * mm, "mid": v(15.83, 3.13) * mm, "end": v(25.65, 16.57) * mm});
            skLineSegment(sketch, "E46", {"start": v(47.52, 37) * mm, "end": v(-47.48, 37) * mm, "construction": true});
            skSolve(sketch);
        }
        {
            var Q0;
            Q0 = qSketchRegion(id + "F1", true);
            var Q1;
            Q1 = qSketchRegion(id + "F0", true);
            extrude(context, id + "F2", {"entities" : qUnion([Q0, Q1]), "depth" : 2000 * mm, "offsetDistance" : 25 * mm});
        }
    });
